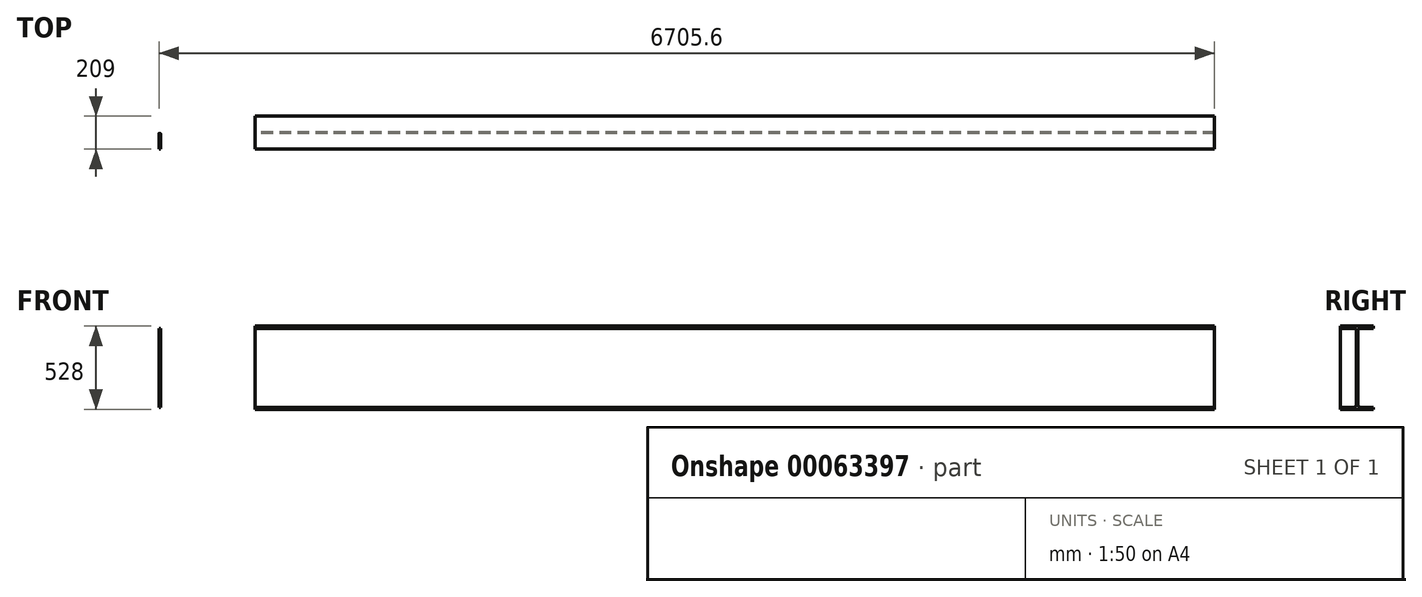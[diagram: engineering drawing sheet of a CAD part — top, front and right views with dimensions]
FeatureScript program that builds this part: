
annotation { "Feature Type Name" : "Feature", "Feature Type Description" : "" }
export const myFeature = defineFeature(function(context is Context, id is Id, definition is map)
    precondition{}
    {
        {
            var Q0;
            Q0=qCreatedBy(makeId("Right.planeOp"),FACE);
            var sketch = newSketch(context, id + "F0", { "sketchPlane" : qUnion([Q0])});
            skLineSegment(sketch, "E0", {"start": v(-4.75, 0) * mm, "end": v(-4.75, 233.99) * mm});
            skLineSegment(sketch, "E1", {"start": v(-21.46, 250.7) * mm, "end": v(-104.5, 250.7) * mm});
            skLineSegment(sketch, "E2", {"start": v(-104.5, 250.7) * mm, "end": v(-104.5, 264) * mm});
            skLineSegment(sketch, "E3", {"start": v(-104.5, 264) * mm, "end": v(0, 264) * mm});
            skPoint(sketch, "E4.visualSharp", {"position": v(-4.75, 250.7) * mm});
            skArc(sketch, "E4.filletArc", {"start": v(-4.75, 233.99) * mm, "mid": v(-9.64, 245.8) * mm, "end": v(-21.46, 250.7) * mm});
            skLineSegment(sketch, "E5.MirrorCS", {"start": v(4.75, 0) * mm, "end": v(4.75, 233.99) * mm});
            skLineSegment(sketch, "E6.MirrorCS", {"start": v(21.46, 250.7) * mm, "end": v(104.5, 250.7) * mm});
            skArc(sketch, "E7.MirrorCS", {"start": v(4.75, 233.99) * mm, "mid": v(9.64, 245.8) * mm, "end": v(21.46, 250.7) * mm});
            skLineSegment(sketch, "E8.MirrorCS", {"start": v(104.5, 264) * mm, "end": v(0, 264) * mm});
            skPoint(sketch, "E9.MirrorP", {"position": v(4.75, 250.7) * mm});
            skLineSegment(sketch, "E10.MirrorCS", {"start": v(104.5, 250.7) * mm, "end": v(104.5, 264) * mm});
            skLineSegment(sketch, "E11.MirrorCS", {"start": v(104.5, -250.7) * mm, "end": v(104.5, -264) * mm});
            skLineSegment(sketch, "E12.MirrorCS", {"start": v(-104.5, -250.7) * mm, "end": v(-104.5, -264) * mm});
            skArc(sketch, "E13.MirrorCS", {"start": v(4.75, -233.99) * mm, "mid": v(9.64, -245.8) * mm, "end": v(21.46, -250.7) * mm});
            skArc(sketch, "E14.MirrorCS", {"start": v(-4.75, -233.99) * mm, "mid": v(-9.64, -245.8) * mm, "end": v(-21.46, -250.7) * mm});
            skPoint(sketch, "E15.MirrorP", {"position": v(4.75, -250.7) * mm});
            skLineSegment(sketch, "E16.MirrorCS", {"start": v(104.5, -264) * mm, "end": v(0, -264) * mm});
            skLineSegment(sketch, "E17.MirrorCS", {"start": v(21.46, -250.7) * mm, "end": v(104.5, -250.7) * mm});
            skLineSegment(sketch, "E18.MirrorCS", {"start": v(4.75, 0) * mm, "end": v(4.75, -233.99) * mm});
            skLineSegment(sketch, "E19.MirrorCS", {"start": v(-21.46, -250.7) * mm, "end": v(-104.5, -250.7) * mm});
            skPoint(sketch, "E20.MirrorP", {"position": v(-4.75, -250.7) * mm});
            skLineSegment(sketch, "E21.MirrorCS", {"start": v(-4.75, 0) * mm, "end": v(-4.75, -233.99) * mm});
            skLineSegment(sketch, "E22.MirrorCS", {"start": v(-104.5, -264) * mm, "end": v(0, -264) * mm});
            skSolve(sketch);
        }
        {
            var Q0;
            Q0=makeQuery(id+"F0.imprint","IMPRINT",FACE,{"disambiguationData":[TD([[makeQuery(id+"F0.imprint","IMPRINT",EDGE,{"derivedFrom":sQuery(id+"F0.wireOp",EDGE,"E0")}),-1.0]])]});
            extrude(context, id + "F1", {"entities" : qUnion([Q0]), "depth" : 6096 * mm});
        }
        {
            var Q0;
            Q0=qCreatedBy(makeId("Right.planeOp"),FACE);
            cPlane(context, id + "F2", {"entities" : qUnion([Q0]), "cplaneType" : CPlaneType.OFFSET, "offset" : 609.6 * mm, "oppositeDirection" : true, "width" : 152.4 * mm, "height" : 152.4 * mm});
        }
        {
            var Q0;
            Q0=qCreatedBy(id+"F2.planeOp",FACE);
            var sketch = newSketch(context, id + "F3", { "sketchPlane" : qUnion([Q0])});
            skLineSegment(sketch, "E23.0", {"start": v(-21.46, 250.7) * mm, "end": v(-104.5, 250.7) * mm});
            skArc(sketch, "E24.0", {"start": v(-4.75, 233.99) * mm, "mid": v(-9.64, 245.8) * mm, "end": v(-21.46, 250.7) * mm});
            skLineSegment(sketch, "E25.0", {"start": v(-4.75, -233.99) * mm, "end": v(-4.75, 233.99) * mm});
            skArc(sketch, "E26.0", {"start": v(-4.75, -233.99) * mm, "mid": v(-9.64, -245.8) * mm, "end": v(-21.46, -250.7) * mm});
            skLineSegment(sketch, "E27.0", {"start": v(-21.46, -250.7) * mm, "end": v(-104.5, -250.7) * mm});
            skLineSegment(sketch, "E28", {"start": v(-104.5, 250.7) * mm, "end": v(-104.5, -250.7) * mm});
            skSolve(sketch);
        }
        {
            var Q0;
            Q0 = qSketchRegion(id + "F3", true);
            extrude(context, id + "F4", {"entities" : qUnion([Q0]), "depth" : 9.52 * mm});
        }
    });
